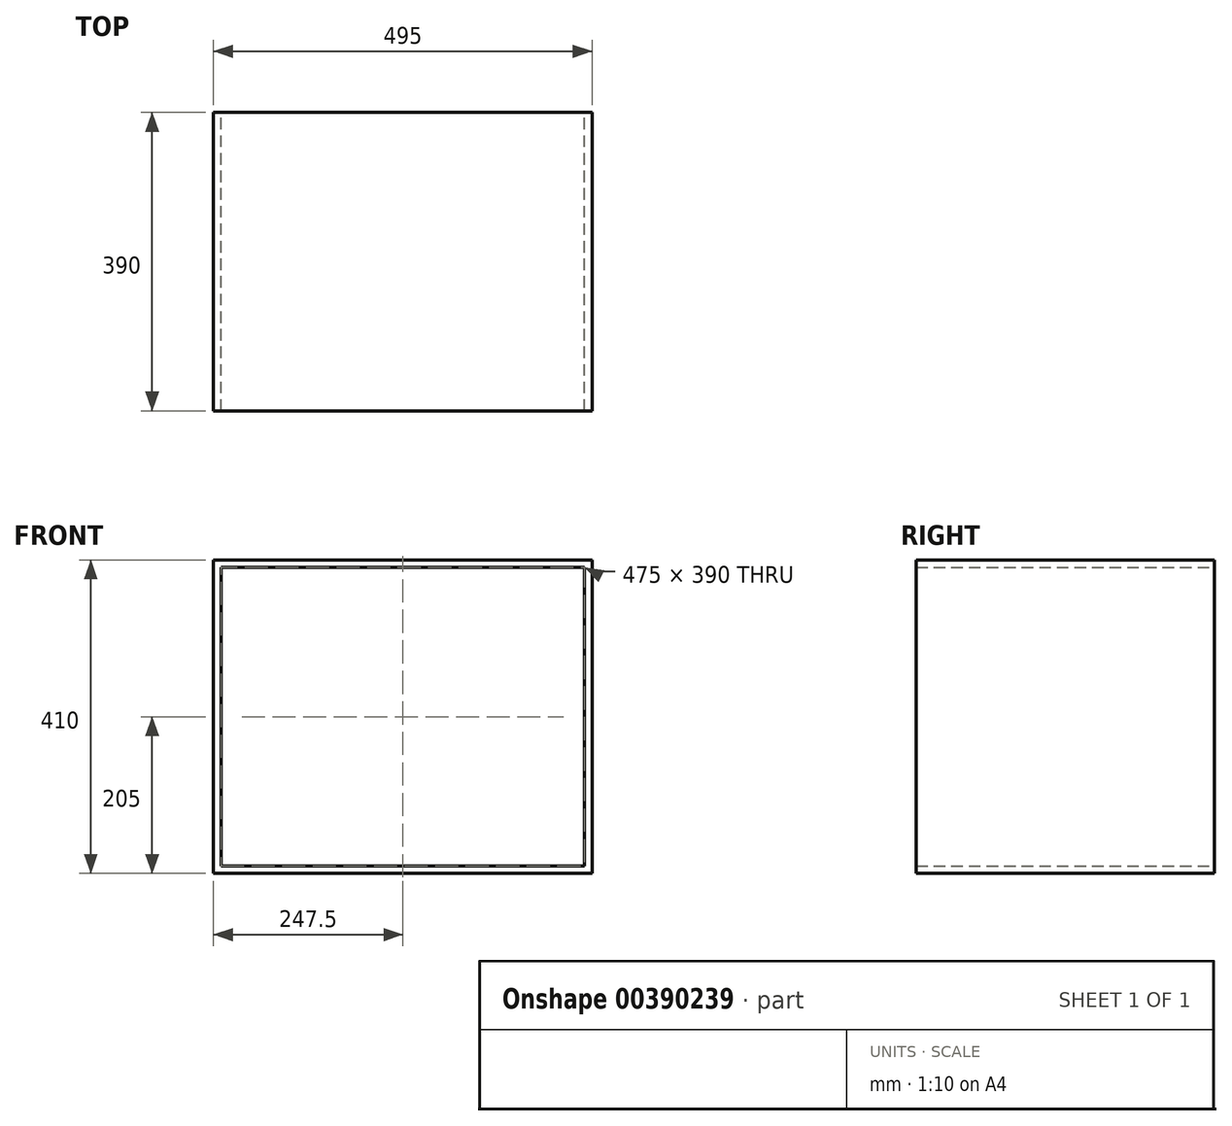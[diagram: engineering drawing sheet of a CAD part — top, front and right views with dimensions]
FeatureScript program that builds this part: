
annotation { "Feature Type Name" : "Feature", "Feature Type Description" : "" }
export const myFeature = defineFeature(function(context is Context, id is Id, definition is map)
    precondition{}
    {
        {
            var Q0;
            Q0=qCreatedBy(makeId("Front.planeOp"),FACE);
            var sketch = newSketch(context, id + "F0", { "sketchPlane" : qUnion([Q0])});
            skLineSegment(sketch, "E0.bottom", {"start": v(247.5, -205) * mm, "end": v(-247.5, -205) * mm});
            skLineSegment(sketch, "E0.top", {"start": v(247.5, 205) * mm, "end": v(-247.5, 205) * mm});
            skLineSegment(sketch, "E0.left", {"start": v(247.5, -205) * mm, "end": v(247.5, 205) * mm});
            skLineSegment(sketch, "E0.right", {"start": v(-247.5, -205) * mm, "end": v(-247.5, 205) * mm});
            skPoint(sketch, "E0.middle", {"position": v(0, 0) * mm});
            skLineSegment(sketch, "E1.bottom", {"start": v(-237.5, 195) * mm, "end": v(237.5, 195) * mm});
            skLineSegment(sketch, "E1.top", {"start": v(-237.5, -195) * mm, "end": v(237.5, -195) * mm});
            skLineSegment(sketch, "E1.left", {"start": v(-237.5, 195) * mm, "end": v(-237.5, -195) * mm});
            skLineSegment(sketch, "E1.right", {"start": v(237.5, 195) * mm, "end": v(237.5, -195) * mm});
            skSolve(sketch);
        }
        {
            var Q0;
            Q0=makeQuery(id+"F0.imprint","IMPRINT",FACE,{"disambiguationData":[TD([[makeQuery(id+"F0.imprint","IMPRINT",EDGE,{"derivedFrom":sQuery(id+"F0.wireOp",EDGE,"E0.bottom")}),-1.0]])]});
            extrude(context, id + "F1", {"entities" : qUnion([Q0]), "depth" : 390 * mm});
        }
    });
